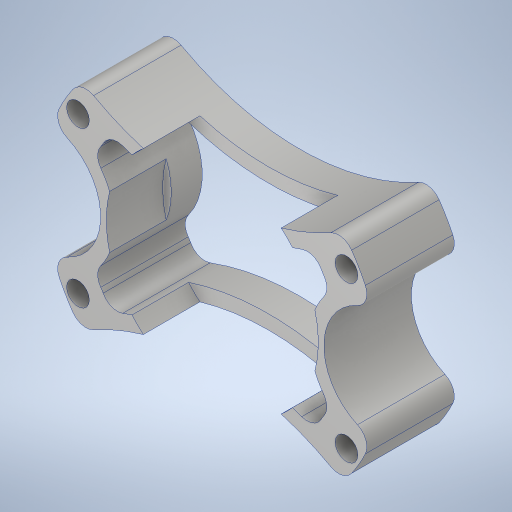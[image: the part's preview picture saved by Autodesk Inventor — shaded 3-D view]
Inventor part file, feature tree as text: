
AUTODESK INVENTOR PART (.ipt)
format: ipt  version: 2023.4 (Build 274418000, 418)  size: 400,384 bytes
history: native  units: in
note: dims shown in document units (in); Inventor stores cm internally (conversion verified against a paired STEP export)
features: sketch x4, extrude x4, fillet x1, hole x1
ambient origin geometry x8: Origin, YZ Plane, XZ Plane, XY Plane, X Axis, Y Axis, Z Axis, Center Point
bodies: Solid1 (feature_tree)
feature tree (10):
  sketch  "Sketch1"  dims[d0=2.375in d1=1.375in d2=0.5in]
  extrude  "Extrusion1"  Depth=0.5in
  fillet  "Fillet1"  Radius=0.5in
  hole  "Hole1"  [1 undecoded]
  extrude  "Extrusion2"  Depth=0.5in
  extrude  "Extrusion3"  Depth=0.5in
  extrude  "Extrusion4"  Depth=0.5in
  sketch  "Sketch3"  dims[d3=0.5in d4=0.5in]
  sketch  "Sketch4"  dims[d5=0.5in d6=1.25in]
  sketch  "Sketch5"  dims[d7=0.5in d8=0.5in d9=0.125in d10=0.125in d11=1.625in d12=0.0in d13=0.14in d14=0.201in d15=0.75in d16=0.385in d17=0.25in d18=0.5635in d19=1.0in d20=0.8108in d21=1.885in d22=0.125in d23=0.0in d24=0.125in d25=0.125in d26=0.125in d27=3.0in d28=1.0in d29=0.851in d30=0.0in d31=1.875in d32=0.1in d33=0.5in d34=0.0in]
note: 1 required parameter value undecoded (feature->parameter linkage not recoverable at this tier; creation-order binding heuristic only, values carry confidence <= 0.55)
